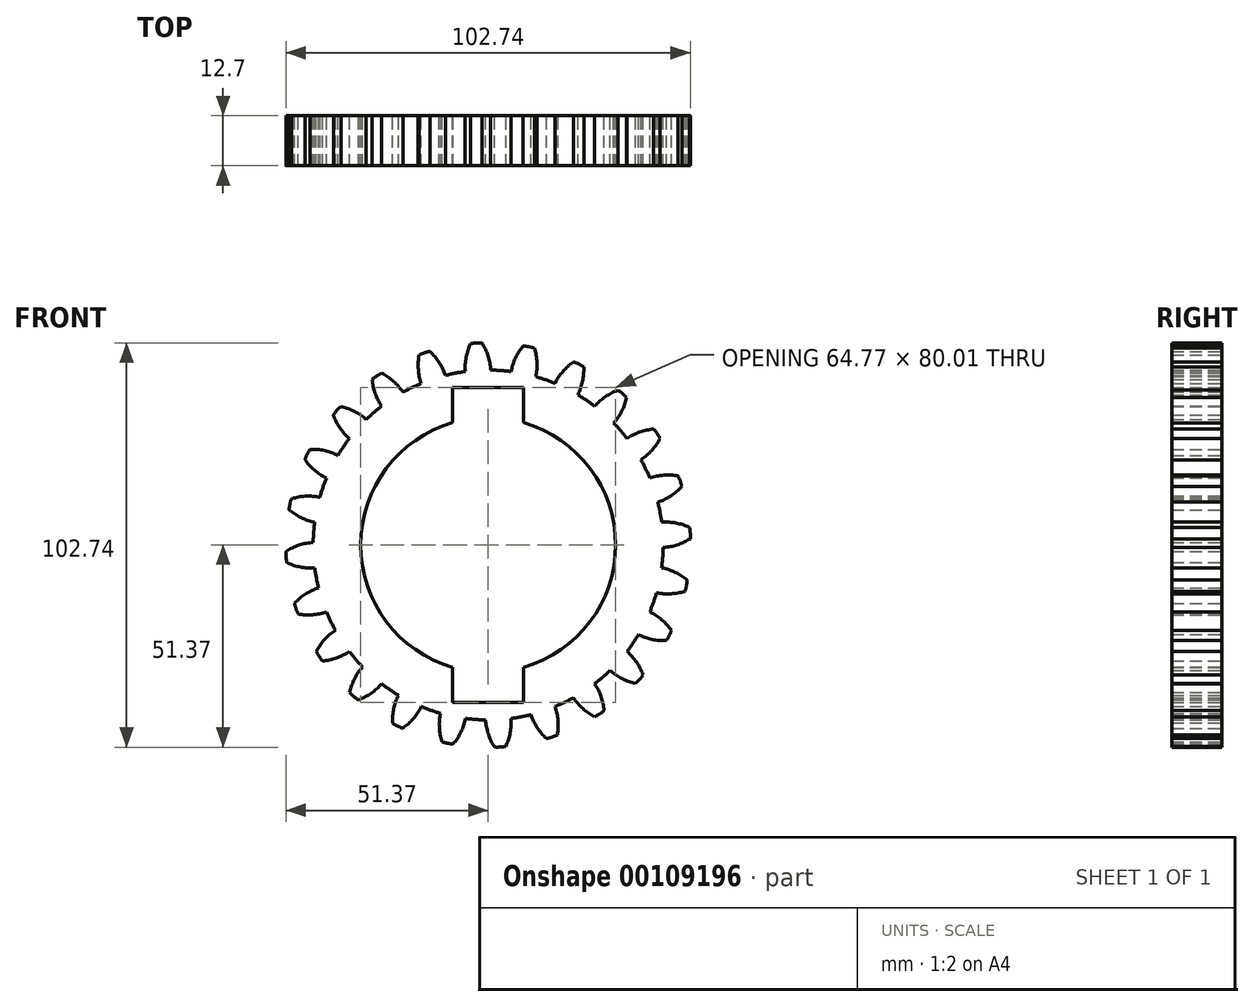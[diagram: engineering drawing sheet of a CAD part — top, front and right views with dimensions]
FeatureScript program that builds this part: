
annotation { "Feature Type Name" : "Feature", "Feature Type Description" : "" }
export const myFeature = defineFeature(function(context is Context, id is Id, definition is map)
    precondition{}
    {
        {
            var Q0;
            Q0=qCreatedBy(makeId("Front.planeOp"),FACE);
            var sketch = newSketch(context, id + "F0", { "sketchPlane" : qUnion([Q0])});
            skCircle(sketch, "E0", {"center": v(0, 0) * mm, "radius": 44.45 * mm});
            skLineSegment(sketch, "E1", {"start": v(0, 56.3) * mm, "end": v(0, -55.83) * mm, "construction": true});
            skCircle(sketch, "E2", {"center": v(0.32, 0) * mm, "radius": 51.37 * mm, "construction": true});
            skCircle(sketch, "E3", {"center": v(0.32, 0) * mm, "radius": 47.93 * mm, "construction": true});
            skCircle(sketch, "E4", {"center": v(0.32, 0) * mm, "radius": 45.8 * mm, "construction": true});
            skLineSegment(sketch, "E5", {"start": v(0.32, 0) * mm, "end": v(-3.35, 56.06) * mm, "construction": true});
            skCircle(sketch, "E6", {"center": v(0, 47.93) * mm, "radius": 14.6 * mm, "construction": true});
            skCircle(sketch, "E7", {"center": v(-13.93, 43.53) * mm, "radius": 14.6 * mm, "construction": true});
            skArc(sketch, "E8", {"start": v(0.65, 44.45) * mm, "mid": v(-0.03, 48.03) * mm, "end": v(-1.59, 51.34) * mm});
            skArc(sketch, "E9.MirrorCS", {"start": v(-5.8, 44.02) * mm, "mid": v(-5.6, 47.67) * mm, "end": v(-4.5, 51.15) * mm});
            skArc(sketch, "E10", {"start": v(-1.59, 51.34) * mm, "mid": v(-3.05, 51.35) * mm, "end": v(-4.5, 51.15) * mm});
            skCircle(sketch, "E11", {"center": v(0, 0) * mm, "radius": 32.39 * mm});
            skLineSegment(sketch, "E12.bottom", {"start": v(-7.87, -39.88) * mm, "end": v(7.52, -39.88) * mm});
            skLineSegment(sketch, "E12.top", {"start": v(-7.87, 39.88) * mm, "end": v(7.52, 39.88) * mm});
            skLineSegment(sketch, "E12.left", {"start": v(-7.87, -39.88) * mm, "end": v(-7.87, 39.88) * mm});
            skLineSegment(sketch, "E12.right", {"start": v(7.52, -39.88) * mm, "end": v(7.52, 39.88) * mm});
            skSolve(sketch);
        }
        {
            var Q0;
            Q0=makeQuery(id+"F0.imprint","IMPRINT",FACE,{"disambiguationData":[TD([[makeQuery(id+"F0.imprint","IMPRINT",EDGE,{"derivedFrom":sQuery(id+"F0.wireOp",EDGE,"E0")}),1.0]])]});
            var Q1;
            {var subQ0=sQuery(id+"F0.wireOp",EDGE,"E8");Q1=makeQuery(id+"F0.imprint","IMPRINT",FACE,{"disambiguationData":[TD([[makeQuery(id+"F0.imprint","IMPRINT",EDGE,{"derivedFrom":subQ0}),1.0]])]});}
            extrude(context, id + "F1", {"entities" : qUnion([Q0, Q1]), "depth" : 12.7 * mm});
        }
        {
            var Q0;
            Q0=makeQuery(id+"F1.opExtrude","SWEPT_BODY",BODY,{"disambiguationData":[OSD([sQuery(id+"F0.wireOp",EDGE,"E0"),sQuery(id+"F0.wireOp",EDGE,"E8"),sQuery(id+"F0.wireOp",EDGE,"E9.MirrorCS"),sQuery(id+"F0.wireOp",EDGE,"E10"),sQuery(id+"F0.wireOp",EDGE,"E11")])]});
            var Q1;
            Q1=makeQuery(id+"F1.opExtrude","SWEPT_FACE",FACE,{"disambiguationData":[OSD([sQuery(id+"F0.wireOp",EDGE,"E0")])]});
            circularPattern(context, id + "F2", {"operationType" : NewBodyOperationType.ADD, "entities" : qUnion([Q0]), "axis" : qUnion([Q1]), "angle" : 15 * degree, "instanceCount" : 24});
        }
        {
            var Q0;
            Q0=qCreatedBy(makeId("Front.planeOp"),FACE);
            var sketch = newSketch(context, id + "F3", { "sketchPlane" : qUnion([Q0])});
            skLineSegment(sketch, "E13.bottom", {"start": v(-9.02, 40) * mm, "end": v(9.02, 40) * mm});
            skLineSegment(sketch, "E13.top", {"start": v(-9.02, -40) * mm, "end": v(9.02, -40) * mm});
            skLineSegment(sketch, "E13.left", {"start": v(-9.02, 40) * mm, "end": v(-9.02, -40) * mm});
            skLineSegment(sketch, "E13.right", {"start": v(9.02, 40) * mm, "end": v(9.02, -40) * mm});
            skSolve(sketch);
        }
        {
            var Q0;
            Q0=qSketchRegion(id+"F3",true);
            var Q1;
            Q1=makeQuery(id+"F3.imprint","IMPRINT",FACE,{"disambiguationData":[TD([[makeQuery(id+"F3.imprint","IMPRINT",EDGE,{"derivedFrom":sQuery(id+"F3.wireOp",EDGE,"E13.bottom")}),-1.0]])]});
            extrude(context, id + "F4", {"entities" : qUnion([Q0, Q1]), "operationType" : NewBodyOperationType.REMOVE, "endBound" : BoundingType.SYMMETRIC, "depth" : 50.8 * mm});
        }
    });
